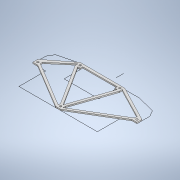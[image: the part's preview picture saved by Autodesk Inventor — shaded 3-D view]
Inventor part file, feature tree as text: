
AUTODESK INVENTOR PART (.ipt)
format: ipt  version: 2020 (Build 240168000, 168)  size: 150,016 bytes
history: native  units: mm
features: other x1, extrude x1, sketch x1
ambient origin geometry x8: Origin, YZ Plane, XZ Plane, XY Plane, X Axis, Y Axis, Z Axis, Center Point
bodies: Solid1 (feature_tree)
feature tree (3):
  other  "TopPlate.dwg"
  extrude  "Extrusion1"  Depth=2.0mm TaperAngle=0.0deg
  sketch  "Sketch1"  dims[d0=3.2mm d1=2.0mm d2=0.0mm]
